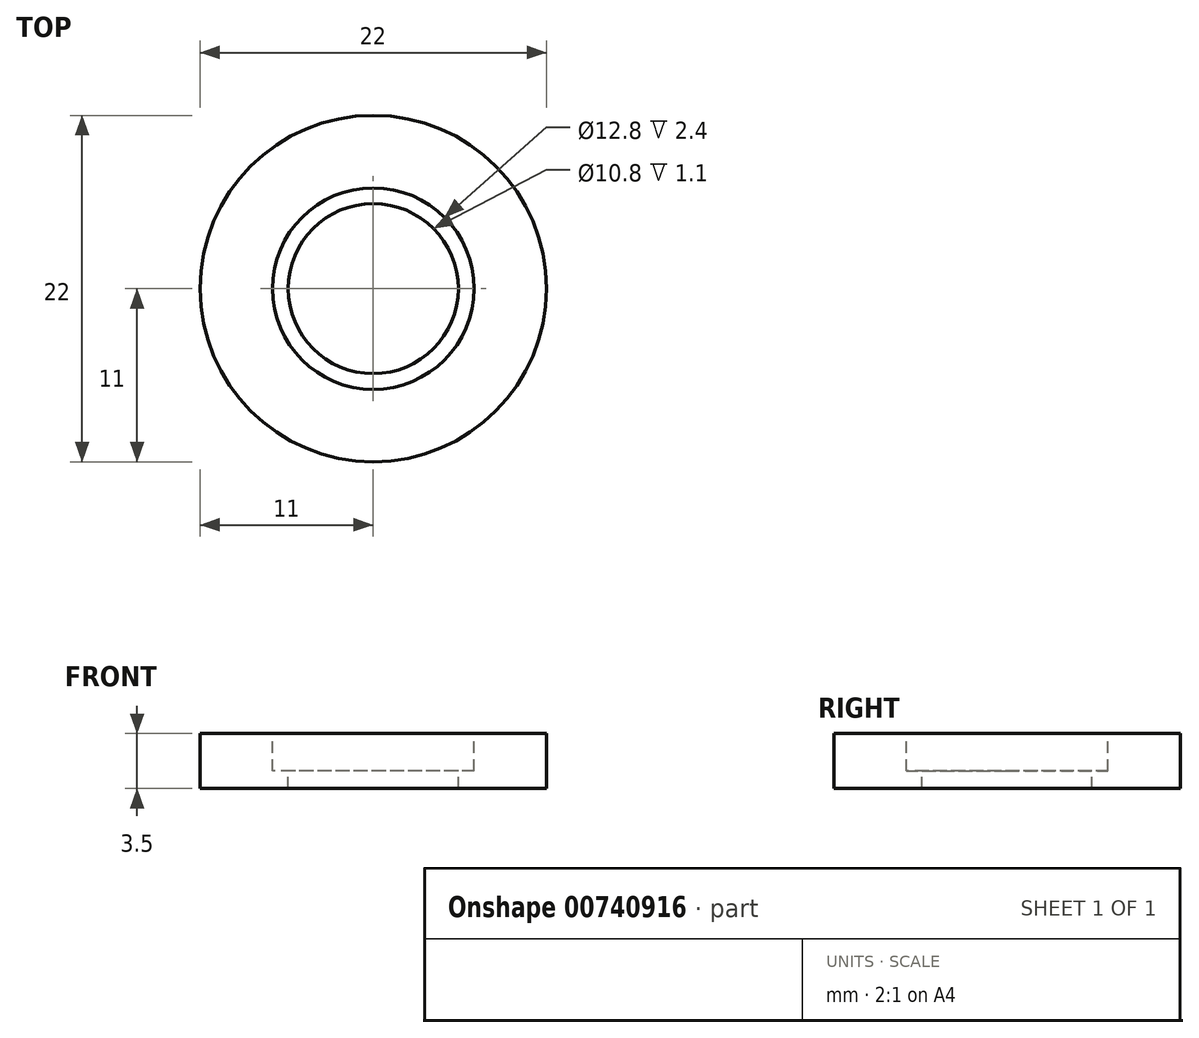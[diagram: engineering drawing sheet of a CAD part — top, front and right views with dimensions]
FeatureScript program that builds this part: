
annotation { "Feature Type Name" : "Feature", "Feature Type Description" : "" }
export const myFeature = defineFeature(function(context is Context, id is Id, definition is map)
    precondition{}
    {
        {
            var Q0;
            Q0=qCreatedBy(makeId("Top.planeOp"),FACE);
            var sketch = newSketch(context, id + "F0", { "sketchPlane" : qUnion([Q0])});
            skCircle(sketch, "E0", {"center": v(0, 0) * mm, "radius": 6.4 * mm});
            skCircle(sketch, "E1", {"center": v(0, 0) * mm, "radius": 11 * mm});
            skSolve(sketch);
        }
        {
            var Q0;
            Q0 = qSketchRegion(id + "F0", true);
            extrude(context, id + "F1", {"entities" : qUnion([Q0]), "oppositeDirection" : true, "depth" : 3.5 * mm, "offsetDistance" : 25 * mm});
        }
        {
            var Q0;
            Q0=qCreatedBy(makeId("Top.planeOp"),FACE);
            cPlane(context, id + "F2", {"entities" : qUnion([Q0]), "cplaneType" : CPlaneType.OFFSET, "offset" : 2.4 * mm, "oppositeDirection" : true, "width" : 150 * mm, "height" : 150 * mm});
        }
        {
            var Q0;
            Q0=qCreatedBy(id+"F2.planeOp",FACE);
            var sketch = newSketch(context, id + "F3", { "sketchPlane" : qUnion([Q0])});
            skCircle(sketch, "E2", {"center": v(0, 0) * mm, "radius": 5.4 * mm});
            skCircle(sketch, "E3.0", {"center": v(0, 0) * mm, "radius": 11 * mm});
            skSolve(sketch);
        }
        {
            var Q0;
            Q0 = qSketchRegion(id + "F3", true);
            var Q1;
            Q1=makeQuery(id+"F1.opExtrude","CAP_FACE",FACE,{"disambiguationData":[OSD([sQuery(id+"F0.wireOp",EDGE,"E0"),sQuery(id+"F0.wireOp",EDGE,"E1")])],"isStart":false});
            extrude(context, id + "F4", {"entities" : qUnion([Q0]), "operationType" : NewBodyOperationType.ADD, "endBound" : BoundingType.UP_TO_SURFACE, "oppositeDirection" : true, "depth" : 25 * mm, "endBoundEntityFace" : qUnion([Q1]), "offsetDistance" : 25 * mm});
        }
    });
